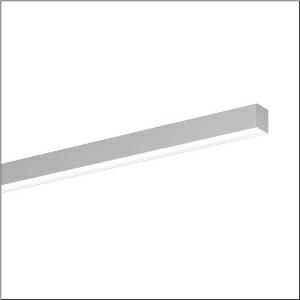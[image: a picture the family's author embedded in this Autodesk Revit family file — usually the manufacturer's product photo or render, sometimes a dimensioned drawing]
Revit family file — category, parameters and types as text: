
# Revit family: silica_r__21_51mx23tat4s_c658
name_source: partatom
category: Lighting Fixtures
units: mm (PartAtom-declared; Revit-internal decimal feet)

## family parameters
Cut with Voids When Loaded = No
Host = Face
Light Source = No
Part Type = Normal
Room Calculation Point = No
Round Connector Dimension = Use Diameter
Shared = No

## types (1)
- --- (1 x LED, 3230 lm, 32.4 W, 6500K)
    Apparent Load = 32 VA
    CIE Flux Codes = 78 96 99 100 100
    Color Rendering = 80
    Color Temperature = 6500K
    Default Elevation = 1800 mm
    Description = Silica® 21, office luminaire, primary optical cover: prismatic diffuser, of PMMA, CAT 2 (L<= 3000cd/m²), light emission: direct distribution, primary light characteristic: symmetric, installation type: surface-mounted, LED, rated luminous flux: 3.230lm, luminous efficacy: 95lm/W, light colour: 8tw, colour temperature: 2700..6500K, control gear: DALI DT8, with terminal, 3+2-pole, max. 2.5mm², mains connection: 220..240V, AC, 50/60Hz, rated input power: 34W, luminaire housing, of aluminium, metallic grey (RAL 9006), length: 1.204mm, width: 53mm, height: 53mm, protection rating (complete): IP20, insulation class (complete): insulation class I (protective earthing), certification: CE, permissible operating ambient temperature: 0..+35°C, standard: EN 50419, packaging unit: 1 piece
    Height = 53 mm
    Lamp = 1 x LED
    Lamp Light Flux = 3230 lm
    Lamp Power = 32.4 W
    Lamp count = 1
    Length = 1204 mm
    Luminous efficacy = 100 lm/W
    Manufacturer = Siteco
    ModVariant = No
    Model = 51MX23TAT4S
    Mounting Place = Ceiling
    Mounting Type = Surface mounted
    Number of Poles = 1
    OnlyDefault = Yes
    Power Factor = 1
    Product Name = Silica® 21
    Product group = office luminaire | ceiling mounted
    ProductGroupID = 303
    Protection Class = Protection class I
    Protection Degree = IP 20
    RLX_Detail_Level = 1
    RLX_Emergency_Light_Flux = 0 lm
    RLX_Emergency_Type = 0
    RLX_Emergency_Type_DB = No
    RlxData = <blob elided: 18013 chars, md5=037a7a2c>
    Socket = socket
    Standby Power = 0 W
    System Light Flux = 3230 lm
    System Power = 32 W
    Type Comments = individual setting
    Type Image = l_1335933.jpg
    URL = http://relux.com
    VarID = @adj_161279
    Voltage = 0 V
    Weight = 0.00 kg
    Width = 53 mm

## geometry (parser evidence)
native form markers: Blend x4, Sweep x11
no freeform markers — native parametric forms only
